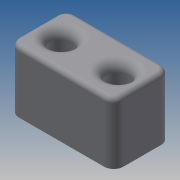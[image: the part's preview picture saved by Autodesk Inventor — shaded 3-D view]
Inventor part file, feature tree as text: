
AUTODESK INVENTOR PART (.ipt)
format: ipt  version: 2014 (Build 180170000, 170)  size: 142,336 bytes
history: native  units: mm
features: fillet x2, extrude x1, sketch x1
ambient origin geometry x8: Origin, YZ Plane, XZ Plane, XY Plane, X Axis, Y Axis, Z Axis, Center Point
bodies: Solid1 (feature_tree)
feature tree (4):
  extrude  "Extrusion1"  Depth=1.0mm
  fillet  "Fillet1"  Radius=12.0mm
  fillet  "Fillet2"  Radius=5.0mm
  sketch  "Sketch1"  dims[d0=12.0mm d1=4.6mm d2=12.0mm d3=5.0mm d4=13.0mm d5=0.0mm d6=2.0mm d7=1.0mm]
